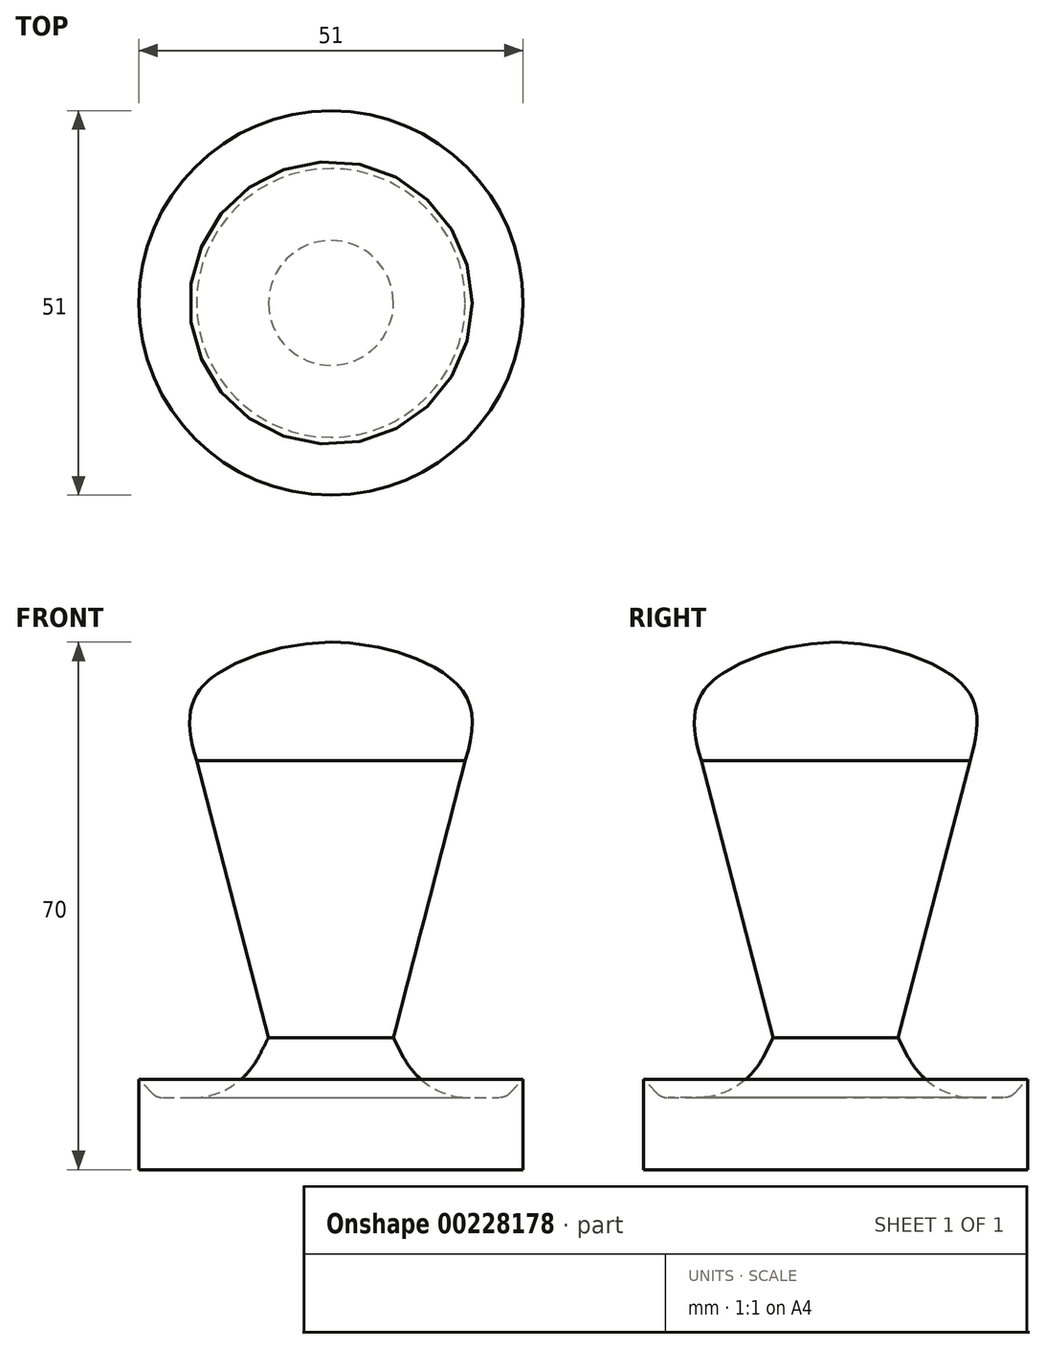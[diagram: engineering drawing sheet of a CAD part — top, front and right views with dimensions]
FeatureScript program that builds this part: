
annotation { "Feature Type Name" : "Feature", "Feature Type Description" : "" }
export const myFeature = defineFeature(function(context is Context, id is Id, definition is map)
    precondition{}
    {
        {
            var Q0;
            Q0=qCreatedBy(makeId("Front.planeOp"),FACE);
            var sketch = newSketch(context, id + "F0", { "sketchPlane" : qUnion([Q0])});
            skLineSegment(sketch, "E0", {"start": v(0, 0) * mm, "end": v(25.5, 0) * mm});
            skLineSegment(sketch, "E1", {"start": v(25.5, 0) * mm, "end": v(25.5, 12) * mm});
            skLineSegment(sketch, "E2", {"start": v(12.43, 9.54) * mm, "end": v(8.29, 17.5) * mm});
            skLineSegment(sketch, "E3", {"start": v(8.29, 17.5) * mm, "end": v(17.84, 54.28) * mm});
            skLineSegment(sketch, "E4", {"start": v(0, 70) * mm, "end": v(0, 0) * mm});
            skLineSegment(sketch, "E5", {"start": v(25.5, 12) * mm, "end": v(23.16, 9.54) * mm});
            skLineSegment(sketch, "E6", {"start": v(23.16, 9.54) * mm, "end": v(12.43, 9.54) * mm});
            skFitSpline(sketch, "E7", {"points": [v(17.84, 54.28) * mm, v(17.9, 62.93) * mm, v(10.03, 68.26) * mm, v(0, 70) * mm], "startDerivative": vector(9.83, 31.96) * mm, "endDerivative": vector(-29.28, 0.6) * mm});
            skSolve(sketch);
        }
        {
            var Q0;
            Q0 = qSketchRegion(id + "F0", true);
            var Q1;
            Q1=sQuery(id+"F0.wireOp",EDGE,"E4");
            revolve(context, id + "F1", {"entities" : qUnion([Q0]), "axis" : qUnion([Q1]), "revolveType" : RevolveType.FULL});
        }
        {
            var Q0;
            Q0=makeQuery(id+"F1.opRevolve","SWEPT_EDGE",EDGE,{"disambiguationData":[OSD([sQuery(id+"F0.wireOp",EDGE,"E2"),sQuery(id+"F0.wireOp",EDGE,"E6")])]});
            var Q1;
            Q1=makeQuery(id+"F1.opRevolve","SWEPT_EDGE",EDGE,{"disambiguationData":[OSD([sQuery(id+"F0.wireOp",EDGE,"E2"),sQuery(id+"F0.wireOp",EDGE,"E6")])]});
            fillet(context, id + "F2", {"entities" : qUnion([Q0, Q1]), "radius" : 10 * mm, "tangentPropagation" : true, "allowEdgeOverflow" : false});
        }
        {
            var Q0;
            Q0=makeQuery(id+"F1.opRevolve","SWEPT_EDGE",EDGE,{"disambiguationData":[OSD([sQuery(id+"F0.wireOp",EDGE,"E5"),sQuery(id+"F0.wireOp",EDGE,"E6")])]});
            fillet(context, id + "F3", {"entities" : qUnion([Q0]), "radius" : 2 * mm, "tangentPropagation" : true, "allowEdgeOverflow" : false});
        }
    });
